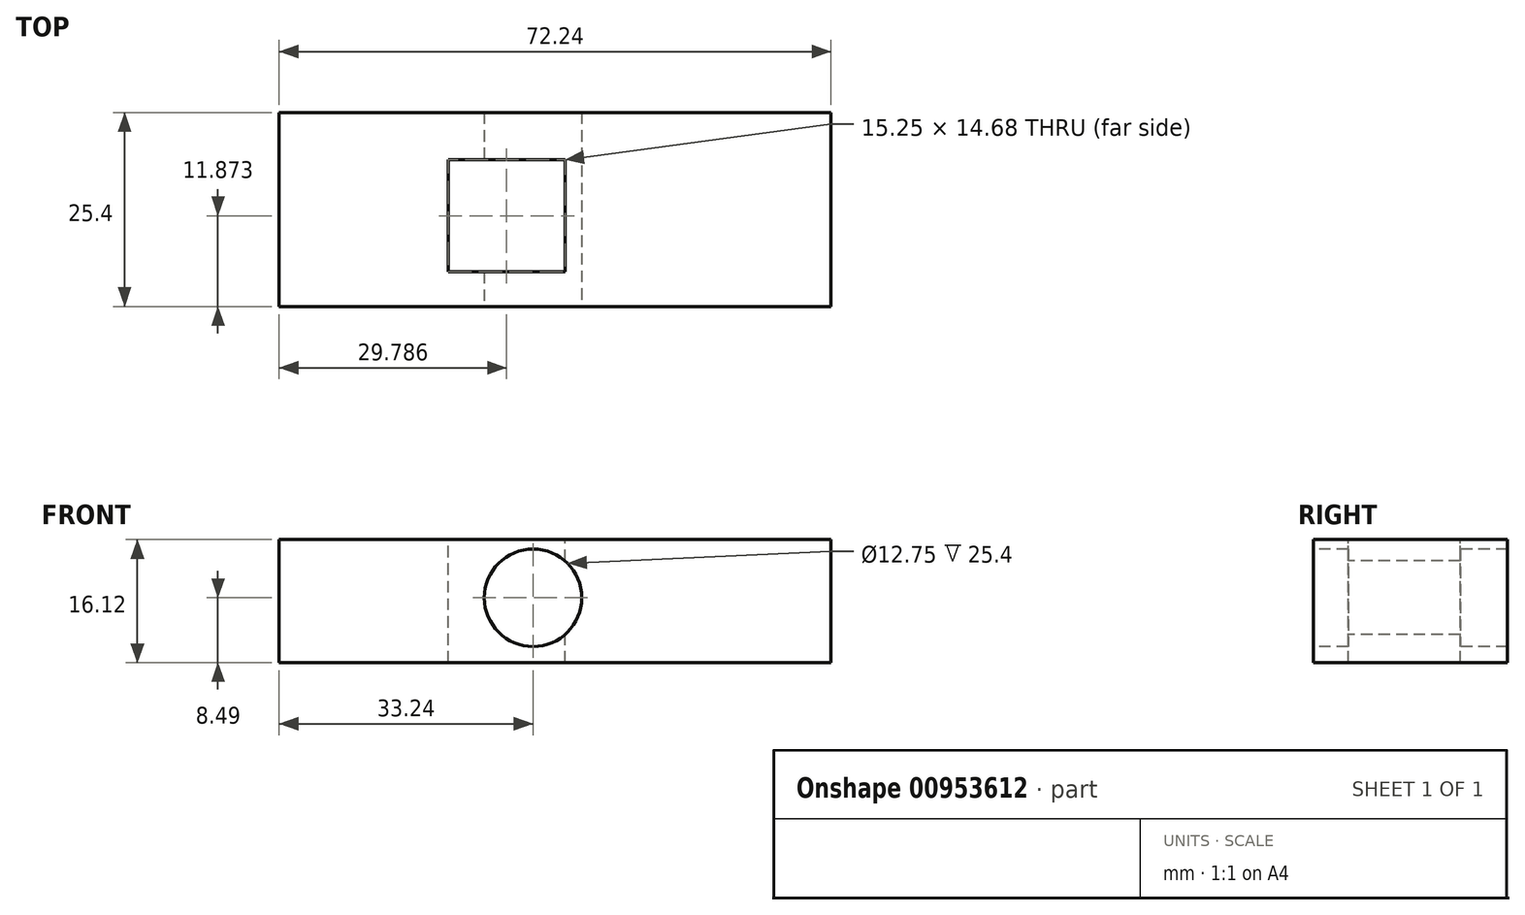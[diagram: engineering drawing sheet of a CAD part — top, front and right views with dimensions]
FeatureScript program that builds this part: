
annotation { "Feature Type Name" : "Feature", "Feature Type Description" : "" }
export const myFeature = defineFeature(function(context is Context, id is Id, definition is map)
    precondition{}
    {
        {
            var Q0;
            Q0=qCreatedBy(makeId("Front.planeOp"),FACE);
            var sketch = newSketch(context, id + "F0", { "sketchPlane" : qUnion([Q0])});
            skLineSegment(sketch, "E0.bottom", {"start": v(-33.24, 7.63) * mm, "end": v(39, 7.63) * mm});
            skLineSegment(sketch, "E0.top", {"start": v(-33.24, -8.5) * mm, "end": v(39, -8.5) * mm});
            skLineSegment(sketch, "E0.left", {"start": v(-33.24, 7.63) * mm, "end": v(-33.24, -8.5) * mm});
            skLineSegment(sketch, "E0.right", {"start": v(39, 7.63) * mm, "end": v(39, -8.5) * mm});
            skSolve(sketch);
        }
        {
            var Q0;
            Q0 = qSketchRegion(id + "F0", true);
            extrude(context, id + "F1", {"entities" : qUnion([Q0]), "depth" : 25.4 * mm, "offsetDistance" : 25.4 * mm});
        }
        {
            var Q0;
            Q0=qCreatedBy(makeId("Top.planeOp"),FACE);
            var sketch = newSketch(context, id + "F2", { "sketchPlane" : qUnion([Q0])});
            skLineSegment(sketch, "E1.bottom", {"start": v(-11.08, -6.19) * mm, "end": v(4.17, -6.19) * mm});
            skLineSegment(sketch, "E1.top", {"start": v(-11.08, -20.87) * mm, "end": v(4.17, -20.87) * mm});
            skLineSegment(sketch, "E1.left", {"start": v(-11.08, -6.19) * mm, "end": v(-11.08, -20.87) * mm});
            skLineSegment(sketch, "E1.right", {"start": v(4.17, -6.19) * mm, "end": v(4.17, -20.87) * mm});
            skSolve(sketch);
        }
        {
            var Q0;
            Q0 = qSketchRegion(id + "F2", true);
            extrude(context, id + "F3", {"entities" : qUnion([Q0]), "operationType" : NewBodyOperationType.REMOVE, "oppositeDirection" : true, "depth" : 50.8 * mm, "offsetDistance" : 25.4 * mm, "hasSecondDirection" : true, "secondDirectionOppositeDirection" : false, "secondDirectionDepth" : 25.4 * mm});
        }
        {
            var Q0;
            Q0=makeQuery(id+"F1.opExtrude","CAP_FACE",FACE,{"disambiguationData":[OSD([sQuery(id+"F0.wireOp",EDGE,"E0.bottom"),sQuery(id+"F0.wireOp",EDGE,"E0.top"),sQuery(id+"F0.wireOp",EDGE,"E0.left"),sQuery(id+"F0.wireOp",EDGE,"E0.right")])],"isStart":false});
            var sketch = newSketch(context, id + "F4", { "sketchPlane" : qUnion([Q0])});
            skSolve(sketch);
        }
        {
            var Q0;
            Q0=makeQuery(id+"F4.imprint","IMPRINT",FACE,{"disambiguationData":[TD([[makeQuery(id+"F4.imprint","IMPRINT",EDGE,{"derivedFrom":makeQuery(id+"F1.opExtrude","CAP_EDGE",EDGE,{"disambiguationData":[OSD([sQuery(id+"F0.wireOp",EDGE,"E0.bottom")])],"isStart":false})}),-1.0]])]});
            var sketch = newSketch(context, id + "F5", { "sketchPlane" : qUnion([Q0])});
            skCircle(sketch, "E2", {"center": v(0, 0) * mm, "radius": 6.37 * mm});
            skSolve(sketch);
        }
        {
            var Q0;
            Q0=makeQuery(id+"F5.imprint","IMPRINT",FACE,{"disambiguationData":[TD([[makeQuery(id+"F5.imprint","IMPRINT",EDGE,{"derivedFrom":sQuery(id+"F5.wireOp",EDGE,"E2")}),1.0]])]});
            var Q1;
            Q1=sQuery(id+"F5.wireOp",EDGE,"E2");
            extrude(context, id + "F6", {"entities" : qUnion([Q0]), "operationType" : NewBodyOperationType.REMOVE, "surfaceEntities" : qUnion([Q1]), "endBound" : BoundingType.THROUGH_ALL, "oppositeDirection" : true, "depth" : 50.8 * mm, "offsetDistance" : 25.4 * mm});
        }
    });
